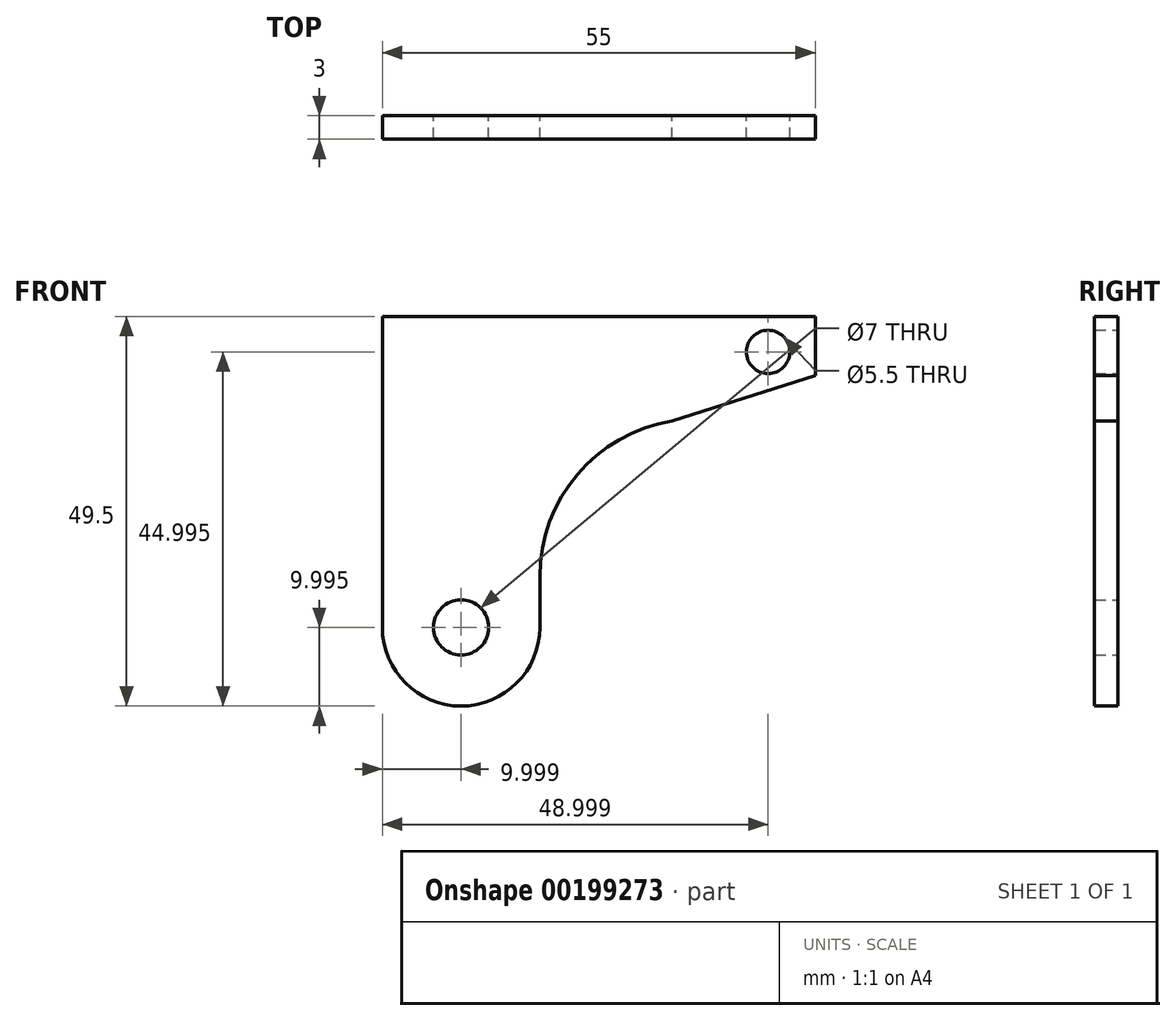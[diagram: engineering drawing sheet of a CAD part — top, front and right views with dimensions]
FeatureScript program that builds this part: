
annotation { "Feature Type Name" : "Feature", "Feature Type Description" : "" }
export const myFeature = defineFeature(function(context is Context, id is Id, definition is map)
    precondition{}
    {
        {
            var Q0;
            Q0=qCreatedBy(makeId("Front.planeOp"),FACE);
            var sketch = newSketch(context, id + "F0", { "sketchPlane" : qUnion([Q0])});
            skLineSegment(sketch, "E0", {"start": v(-14.16, 26.16) * mm, "end": v(40.84, 26.16) * mm});
            skLineSegment(sketch, "E1", {"start": v(40.84, 26.16) * mm, "end": v(40.84, 18.66) * mm});
            skLineSegment(sketch, "E2", {"start": v(-14.16, 26.16) * mm, "end": v(-14.16, -13.34) * mm});
            skArc(sketch, "E3", {"start": v(-14.16, -13.34) * mm, "mid": v(-4.16, -23.34) * mm, "end": v(5.84, -13.34) * mm});
            skLineSegment(sketch, "E4", {"start": v(5.84, -13.34) * mm, "end": v(5.84, -6.87) * mm});
            skArc(sketch, "E5", {"start": v(22.62, 12.86) * mm, "mid": v(10.6, 6.08) * mm, "end": v(5.84, -6.87) * mm});
            skCircle(sketch, "E6", {"center": v(-4.16, -13.34) * mm, "radius": 3.5 * mm});
            skLineSegment(sketch, "E7", {"start": v(40.84, 18.66) * mm, "end": v(22.62, 12.86) * mm});
            skCircle(sketch, "E8", {"center": v(34.84, 21.66) * mm, "radius": 2.75 * mm});
            skSolve(sketch);
        }
        {
            var Q0;
            Q0=qSketchRegion(id+"F0",true);
            extrude(context, id + "F1", {"entities" : qUnion([Q0]), "depth" : 3 * mm});
        }
    });
